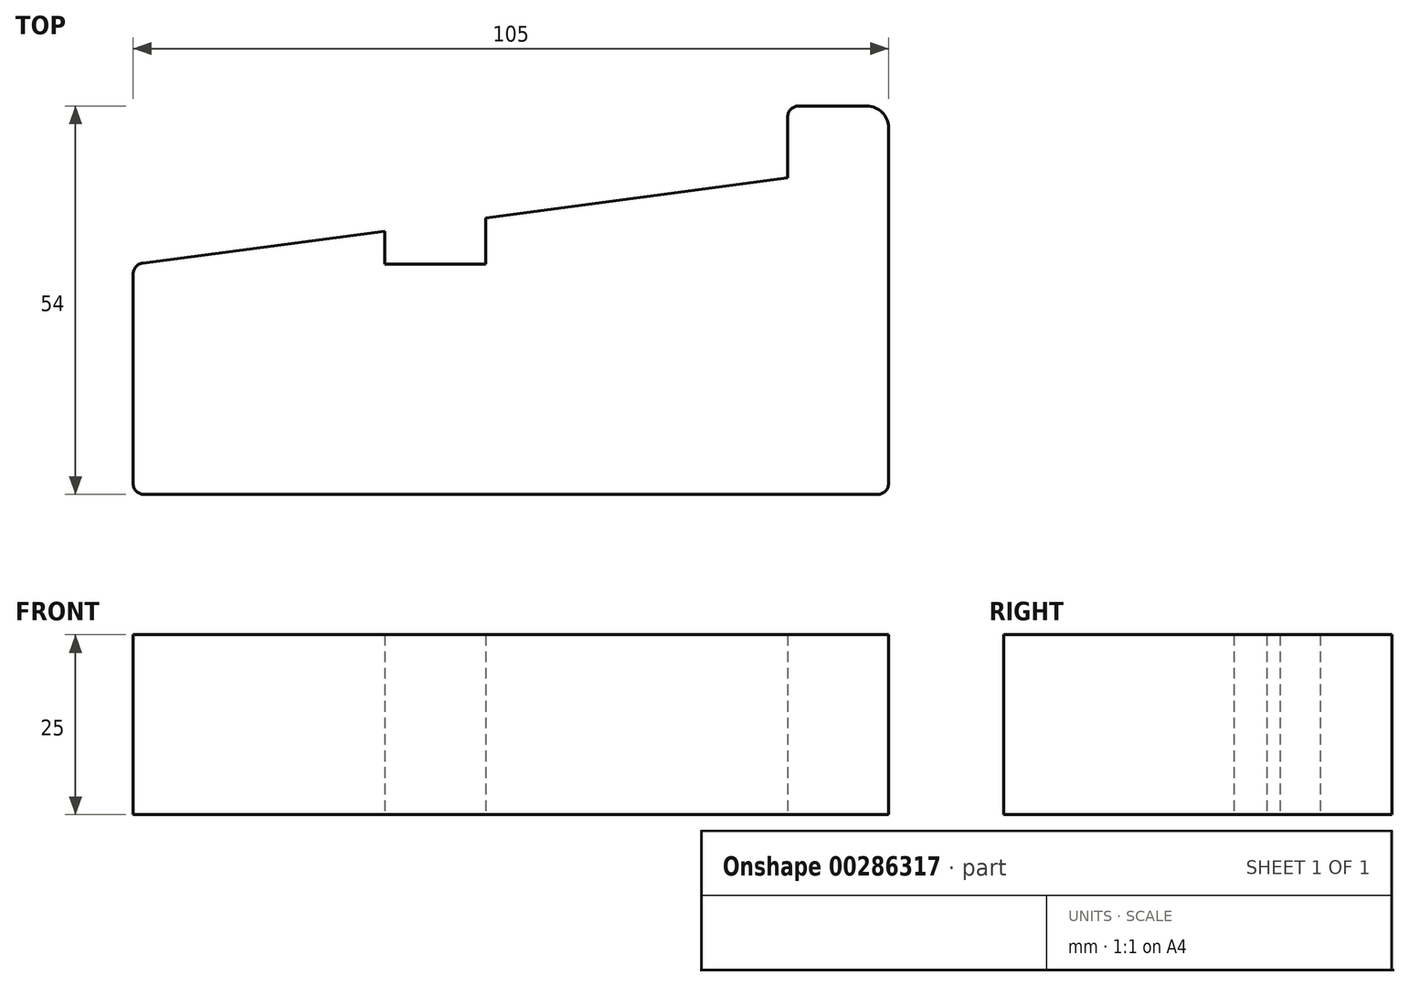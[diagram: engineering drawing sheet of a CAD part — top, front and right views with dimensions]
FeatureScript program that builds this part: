
annotation { "Feature Type Name" : "Feature", "Feature Type Description" : "" }
export const myFeature = defineFeature(function(context is Context, id is Id, definition is map)
    precondition{}
    {
        {
            var Q0;
            Q0=qCreatedBy(makeId("Top.planeOp"),FACE);
            var sketch = newSketch(context, id + "F0", { "sketchPlane" : qUnion([Q0])});
            skLineSegment(sketch, "E0", {"start": v(-47.22, -47.15) * mm, "end": v(54.78, -47.15) * mm});
            skLineSegment(sketch, "E1", {"start": v(56.28, -45.65) * mm, "end": v(56.28, 3.85) * mm});
            skLineSegment(sketch, "E2", {"start": v(53.28, 6.85) * mm, "end": v(43.78, 6.85) * mm});
            skLineSegment(sketch, "E3", {"start": v(42.28, 5.35) * mm, "end": v(42.28, -3.15) * mm});
            skLineSegment(sketch, "E4", {"start": v(42.28, -3.15) * mm, "end": v(0.28, -8.69) * mm});
            skLineSegment(sketch, "E5", {"start": v(-48.72, -16.46) * mm, "end": v(-48.72, -45.65) * mm});
            skLineSegment(sketch, "E6", {"start": v(-13.72, -15.15) * mm, "end": v(0.28, -15.15) * mm});
            skLineSegment(sketch, "E7", {"start": v(-13.72, -15.15) * mm, "end": v(-13.72, -10.53) * mm});
            skLineSegment(sketch, "E8", {"start": v(0.28, -15.15) * mm, "end": v(0.28, -8.69) * mm});
            skLineSegment(sketch, "E9.trimOffspring", {"start": v(-13.72, -10.53) * mm, "end": v(-47.42, -14.98) * mm});
            skPoint(sketch, "E10.visualSharp", {"position": v(56.28, 6.85) * mm});
            skArc(sketch, "E10.filletArc", {"start": v(56.28, 3.85) * mm, "mid": v(55.4, 5.97) * mm, "end": v(53.28, 6.85) * mm});
            skPoint(sketch, "E11.visualSharp", {"position": v(-48.72, -47.15) * mm});
            skArc(sketch, "E11.filletArc", {"start": v(-48.72, -45.65) * mm, "mid": v(-48.28, -46.7) * mm, "end": v(-47.22, -47.15) * mm});
            skPoint(sketch, "E12.visualSharp", {"position": v(-48.72, -15.15) * mm});
            skArc(sketch, "E12.filletArc", {"start": v(-47.42, -14.98) * mm, "mid": v(-48.35, -15.47) * mm, "end": v(-48.72, -16.46) * mm});
            skPoint(sketch, "E13.visualSharp", {"position": v(56.28, -47.15) * mm});
            skArc(sketch, "E13.filletArc", {"start": v(54.78, -47.15) * mm, "mid": v(55.84, -46.7) * mm, "end": v(56.28, -45.65) * mm});
            skPoint(sketch, "E14.visualSharp", {"position": v(42.28, 6.85) * mm});
            skArc(sketch, "E14.filletArc", {"start": v(43.78, 6.85) * mm, "mid": v(42.72, 6.41) * mm, "end": v(42.28, 5.35) * mm});
            skSolve(sketch);
        }
        {
            var Q0;
            Q0=makeQuery(id+"F0.imprint","IMPRINT",FACE,{"disambiguationData":[TD([[makeQuery(id+"F0.imprint","IMPRINT",EDGE,{"derivedFrom":sQuery(id+"F0.wireOp",EDGE,"E0")}),1.0]])]});
            extrude(context, id + "F1", {"entities" : qUnion([Q0]), "depth" : 25 * mm});
        }
    });
